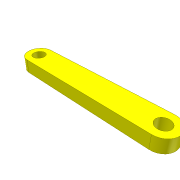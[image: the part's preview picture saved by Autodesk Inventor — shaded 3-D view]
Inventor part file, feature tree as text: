
AUTODESK INVENTOR PART (.ipt)
format: ipt  version: unknown  size: 167,424 bytes
history: native  units: mm
features: extrude x1, sketch x1
ambient origin geometry x8: Origin, YZ Plane, XZ Plane, XY Plane, X Axis, Y Axis, Z Axis, Center Point
feature tree (2):
  extrude  "Extrusion1"  Depth=2.0mm
  sketch  "Sketch1"  dims[d0=1.0mm d1=2.0mm d2=10.0mm d3=1.0mm d4=2.0mm d6=1.0mm d7=0.0mm]
